# Revit family: HOMECARE ASSIST SINK MIXER
name_source: partatom
category: Plumbing Fixtures
units: mm (PartAtom-declared; Revit-internal decimal feet)

## family parameters
Cut with Voids When Loaded = Yes
Host = Face
OmniClass Number = 23.45.55.17
OmniClass Title = Mixing Faucets
Part Type = Normal
Room Calculation Point = No
Round Connector Dimension = Use Diameter
Shared = No

## types (3) — shared parameters
Assembly Code = D2020300
CW Connection = Yes
HW Connection = Yes
Manufacturer = GWA Bathrooms & Kitchens
URL = https://www.caroma.com.au
Vent Connection = No
Waste Connection = No
zero-valued in all types: Default Elevation

## per-type parameters (varying)
| type | Base_Material | Model |
| HOMECARE ASSIST SINK MIXER CH LF | GWA_Metal-Chrome | 98273C4AF |
| HOMECARE ASSIST SINK MIXER BLK LF | GWA-Metal-Black | 98273B4AF |
| HOMECARE ASSIST SINK MIXER BN LF | GWA_Metal-Brushed-Nickel | 98273BN4AF |

note: column(s) folded — value = type name in every type: Description

## geometry (parser evidence)
native form markers: Sweep x4
no freeform markers — native parametric forms only
